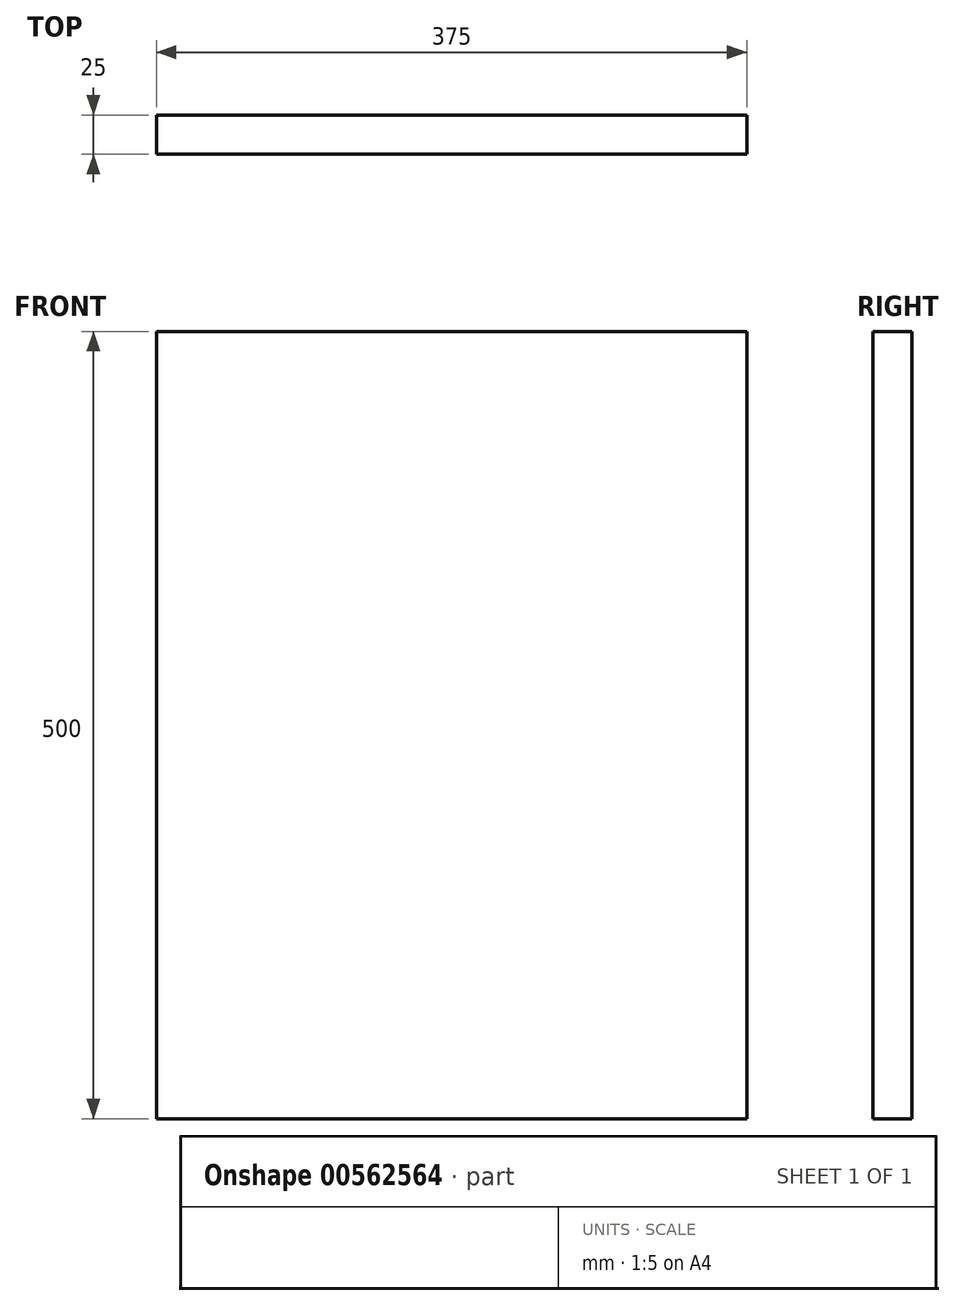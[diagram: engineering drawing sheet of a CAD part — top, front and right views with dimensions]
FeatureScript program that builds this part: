
annotation { "Feature Type Name" : "Feature", "Feature Type Description" : "" }
export const myFeature = defineFeature(function(context is Context, id is Id, definition is map)
    precondition{}
    {
        {
            var Q0;
            Q0=qCreatedBy(makeId("Front.planeOp"),FACE);
            var sketch = newSketch(context, id + "F0", { "sketchPlane" : qUnion([Q0])});
            skLineSegment(sketch, "E0.bottom", {"start": v(0, 0) * mm, "end": v(375, 0) * mm});
            skLineSegment(sketch, "E0.top", {"start": v(0, 500) * mm, "end": v(375, 500) * mm});
            skLineSegment(sketch, "E0.left", {"start": v(0, 0) * mm, "end": v(0, 500) * mm});
            skLineSegment(sketch, "E0.right", {"start": v(375, 0) * mm, "end": v(375, 500) * mm});
            skSolve(sketch);
        }
        {
            var Q0;
            Q0=qSketchRegion(id+"F0",true);
            var Q1;
            Q1=makeQuery(id+"F0.imprint","IMPRINT",FACE,{"disambiguationData":[TD([[makeQuery(id+"F0.imprint","IMPRINT",EDGE,{"derivedFrom":sQuery(id+"F0.wireOp",EDGE,"E0.bottom")}),1.0]])]});
            extrude(context, id + "F1", {"entities" : qUnion([Q0, Q1]), "depth" : 25 * mm, "offsetDistance" : 25 * mm});
        }
    });
